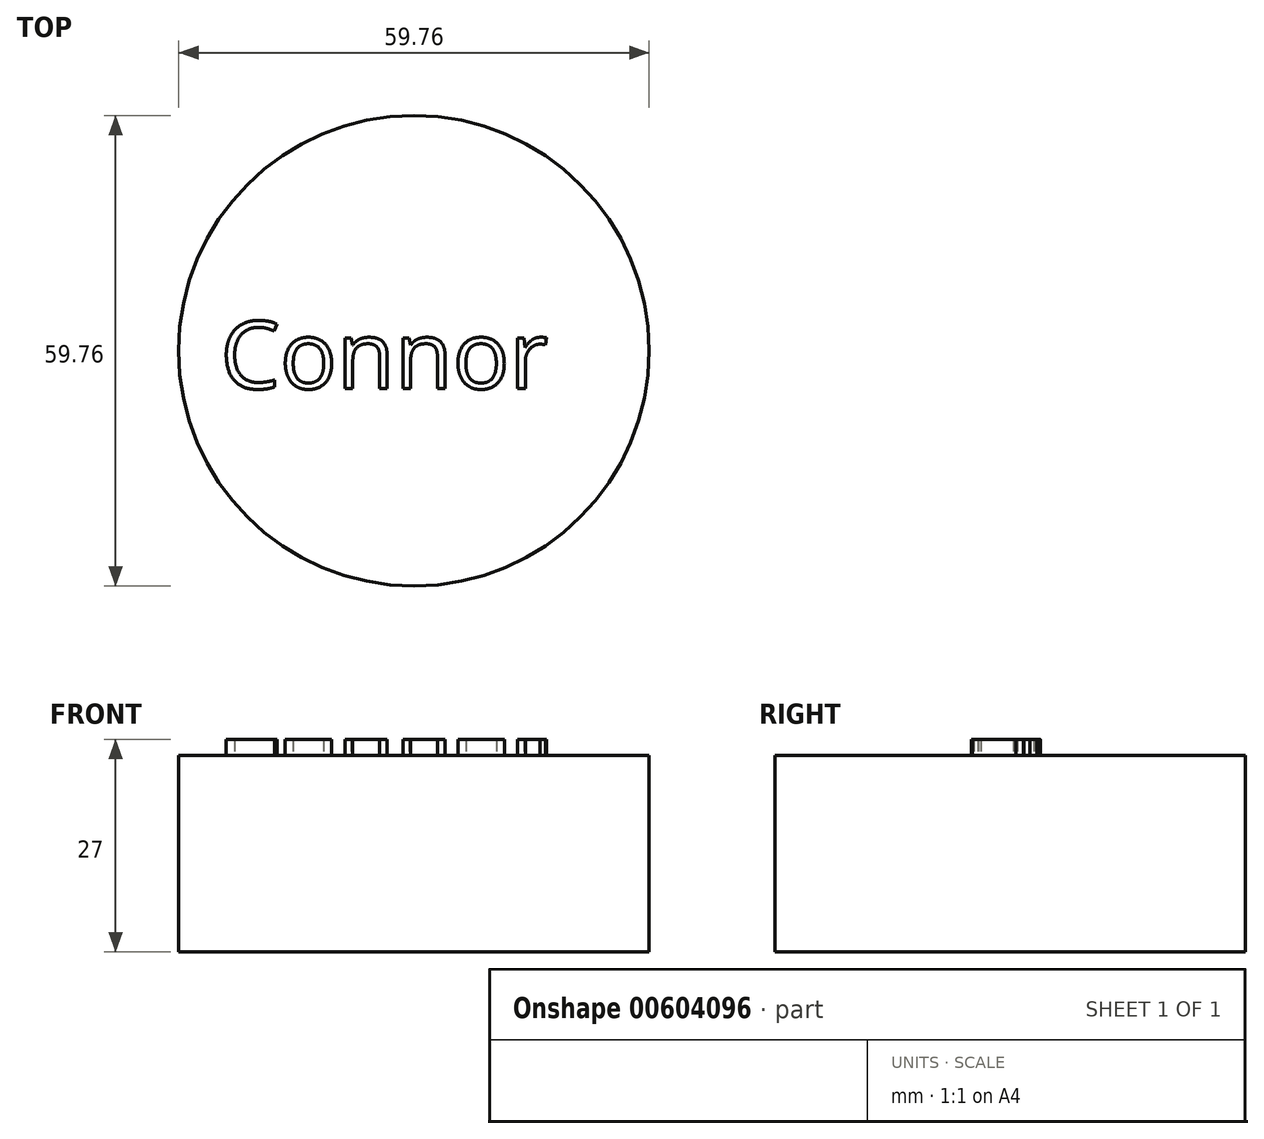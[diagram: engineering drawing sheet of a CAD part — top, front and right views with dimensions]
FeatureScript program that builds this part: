
annotation { "Feature Type Name" : "Feature", "Feature Type Description" : "" }
export const myFeature = defineFeature(function(context is Context, id is Id, definition is map)
    precondition{}
    {
        {
            var Q0;
            Q0=qCreatedBy(makeId("Top.planeOp"),FACE);
            var sketch = newSketch(context, id + "F0", { "sketchPlane" : qUnion([Q0])});
            skCircle(sketch, "E0", {"center": v(0, 0) * mm, "radius": 29.88 * mm});
            skSolve(sketch);
        }
        {
            var Q0;
            Q0 = qSketchRegion(id + "F0", true);
            extrude(context, id + "F1", {"entities" : qUnion([Q0]), "depth" : 25 * mm, "offsetDistance" : 25 * mm});
        }
        {
            var Q0;
            Q0=makeQuery(id+"F1.opExtrude","CAP_FACE",FACE,{"disambiguationData":[OSD([sQuery(id+"F0.wireOp",EDGE,"E0")])],"isStart":false});
            var sketch = newSketch(context, id + "F2", { "sketchPlane" : qUnion([Q0])});
            skText(sketch, "E1", { "text": "Connor", "fontName": "OpenSans-Regular.ttf"});
            const initialGuessF2  = {"E1": [-0.02456, -0.00481, 1, 0, 0.00862]};
            skSetInitialGuess(sketch, initialGuessF2);
            skSolve(sketch);
        }
        {
            var Q0;
            Q0 = qSketchRegion(id + "F2", true);
            extrude(context, id + "F3", {"entities" : qUnion([Q0]), "operationType" : NewBodyOperationType.ADD, "depth" : 2 * mm, "offsetDistance" : 25 * mm});
        }
        {
            var Q0;
            {var subQ0=sQuery(id+"F0.wireOp",EDGE,"E0");Q0=makeQuery(id+"F3.boolean.opBoolean","SPLIT",FACE,{"disambiguationData":[TD([makeQuery(id+"F1.opExtrude","SWEPT_FACE",FACE,{"disambiguationData":[OSD([subQ0])]})])],"derivedFrom":makeQuery(id+"F1.opExtrude","CAP_FACE",FACE,{"disambiguationData":[OSD([subQ0])],"isStart":false})});}
            var sketch = newSketch(context, id + "F4", { "sketchPlane" : qUnion([Q0])});
            skLineSegment(sketch, "E2", {"start": v(25.33, -15.86) * mm, "end": v(30, -20.2) * mm});
            skLineSegment(sketch, "E3", {"start": v(-26.22, -14.34) * mm, "end": v(-32.06, -18.35) * mm});
            skSolve(sketch);
        }
        {
            var Q0;
            Q0=sQuery(id+"F4.wireOp",EDGE,"E2");
            extrude(context, id + "F5", {"bodyType" : ToolBodyType.SURFACE, "surfaceEntities" : qUnion([Q0]), "depth" : 25 * mm, "offsetDistance" : 25 * mm});
        }
    });
